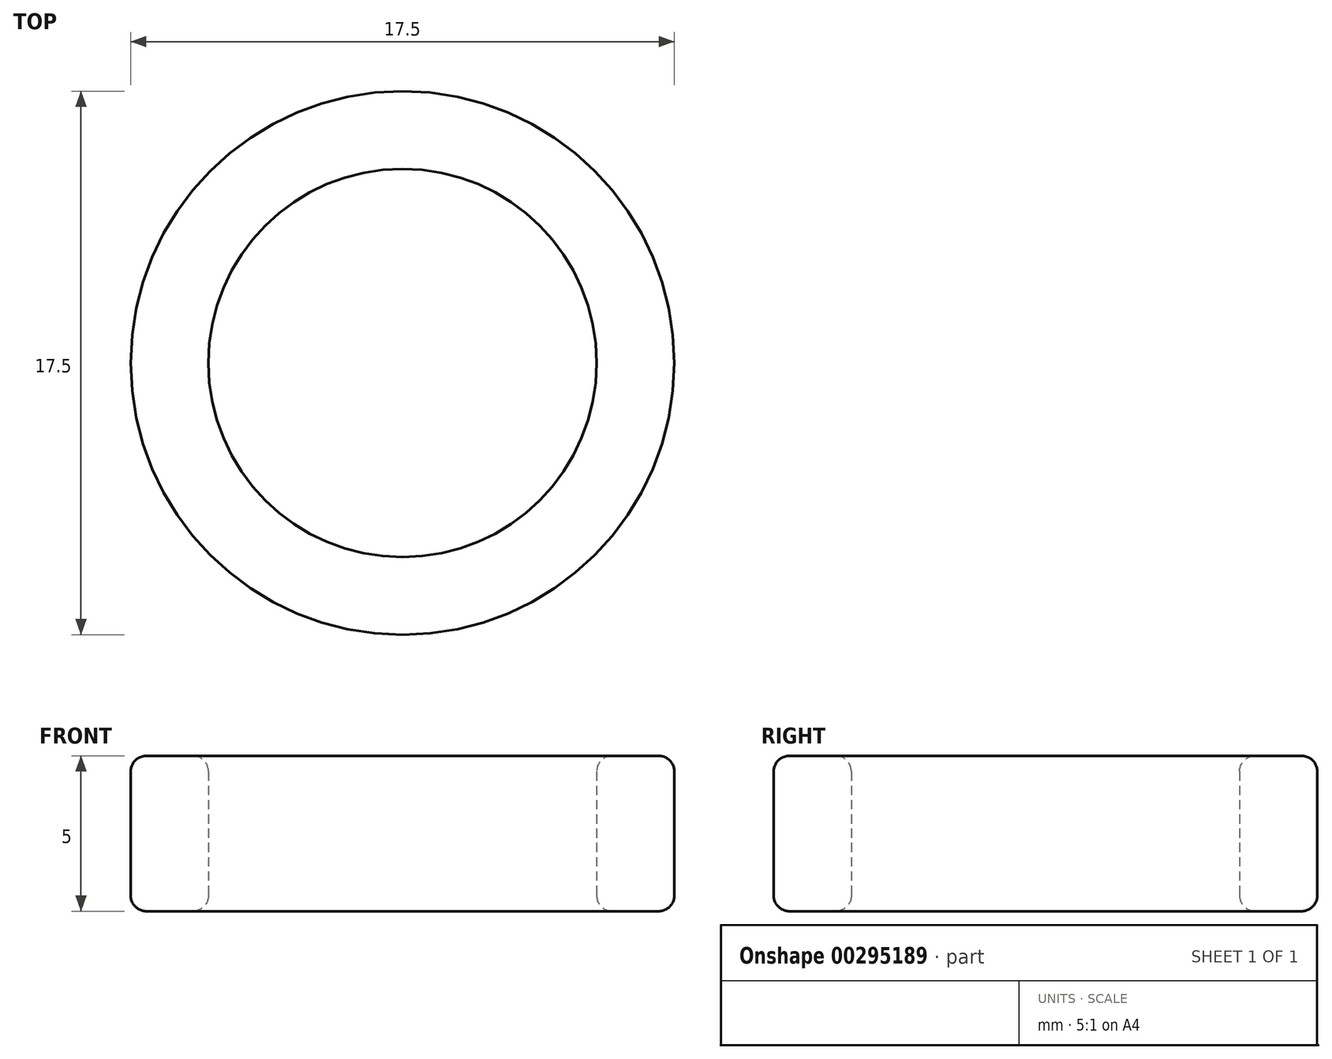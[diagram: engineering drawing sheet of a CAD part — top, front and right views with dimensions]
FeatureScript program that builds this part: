
annotation { "Feature Type Name" : "Feature", "Feature Type Description" : "" }
export const myFeature = defineFeature(function(context is Context, id is Id, definition is map)
    precondition{}
    {
        {
            var Q0;
            Q0=qCreatedBy(makeId("Top.planeOp"),FACE);
            var sketch = newSketch(context, id + "F0", { "sketchPlane" : qUnion([Q0])});
            skCircle(sketch, "E0", {"center": v(0, 0) * mm, "radius": 6.25 * mm});
            skCircle(sketch, "E1", {"center": v(0, 0) * mm, "radius": 8.75 * mm});
            skSolve(sketch);
        }
        {
            var Q0;
            Q0=qSketchRegion(id+"F0",true);
            extrude(context, id + "F1", {"entities" : qUnion([Q0]), "depth" : 5 * mm});
        }
        {
            var Q0;
            Q0=makeQuery(id+"F1.opExtrude","CAP_EDGE",EDGE,{"disambiguationData":[OSD([sQuery(id+"F0.wireOp",EDGE,"E1")])],"isStart":true});
            var Q1;
            Q1=makeQuery(id+"F1.opExtrude","CAP_EDGE",EDGE,{"disambiguationData":[OSD([sQuery(id+"F0.wireOp",EDGE,"E1")])],"isStart":false});
            fillet(context, id + "F2", {"entities" : qUnion([Q0, Q1]), "radius" : 0.5 * mm, "tangentPropagation" : true, "allowEdgeOverflow" : false});
        }
        {
            var Q0;
            Q0=makeQuery(id+"F1.opExtrude","CAP_EDGE",EDGE,{"disambiguationData":[OSD([sQuery(id+"F0.wireOp",EDGE,"E0")])],"isStart":true});
            var Q1;
            Q1=makeQuery(id+"F1.opExtrude","CAP_EDGE",EDGE,{"disambiguationData":[OSD([sQuery(id+"F0.wireOp",EDGE,"E0")])],"isStart":false});
            fillet(context, id + "F3", {"entities" : qUnion([Q0, Q1]), "radius" : 0.5 * mm, "tangentPropagation" : true, "allowEdgeOverflow" : false});
        }
    });
